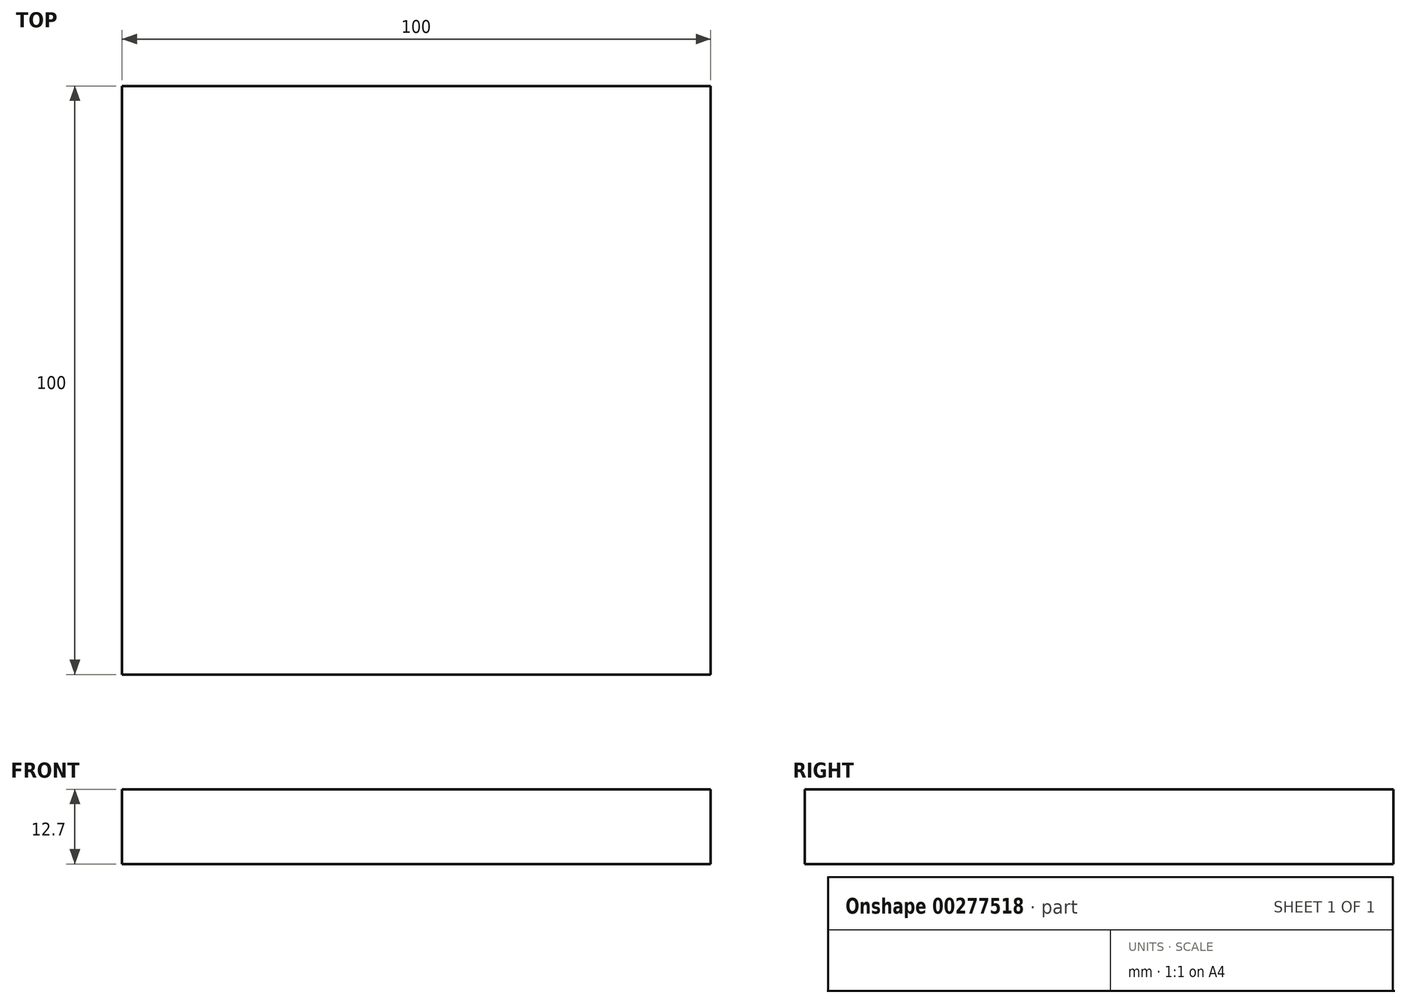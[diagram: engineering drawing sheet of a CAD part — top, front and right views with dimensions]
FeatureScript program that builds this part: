
annotation { "Feature Type Name" : "Feature", "Feature Type Description" : "" }
export const myFeature = defineFeature(function(context is Context, id is Id, definition is map)
    precondition{}
    {
        {
            var Q0;
            Q0=qCreatedBy(makeId("Top.planeOp"),FACE);
            var sketch = newSketch(context, id + "F0", { "sketchPlane" : qUnion([Q0])});
            skLineSegment(sketch, "E0.bottom", {"start": v(50, 50) * mm, "end": v(-50, 50) * mm});
            skLineSegment(sketch, "E0.top", {"start": v(50, -50) * mm, "end": v(-50, -50) * mm});
            skLineSegment(sketch, "E0.left", {"start": v(50, 50) * mm, "end": v(50, -50) * mm});
            skLineSegment(sketch, "E0.right", {"start": v(-50, 50) * mm, "end": v(-50, -50) * mm});
            skPoint(sketch, "E0.middle", {"position": v(0, 0) * mm});
            skSolve(sketch);
        }
        {
            var Q0;
            Q0=makeQuery(id+"F0.imprint","IMPRINT",FACE,{"disambiguationData":[TD([[makeQuery(id+"F0.imprint","IMPRINT",EDGE,{"derivedFrom":sQuery(id+"F0.wireOp",EDGE,"E0.bottom")}),1.0]])]});
            extrude(context, id + "F1", {"entities" : qUnion([Q0]), "depth" : 12.7 * mm});
        }
    });
